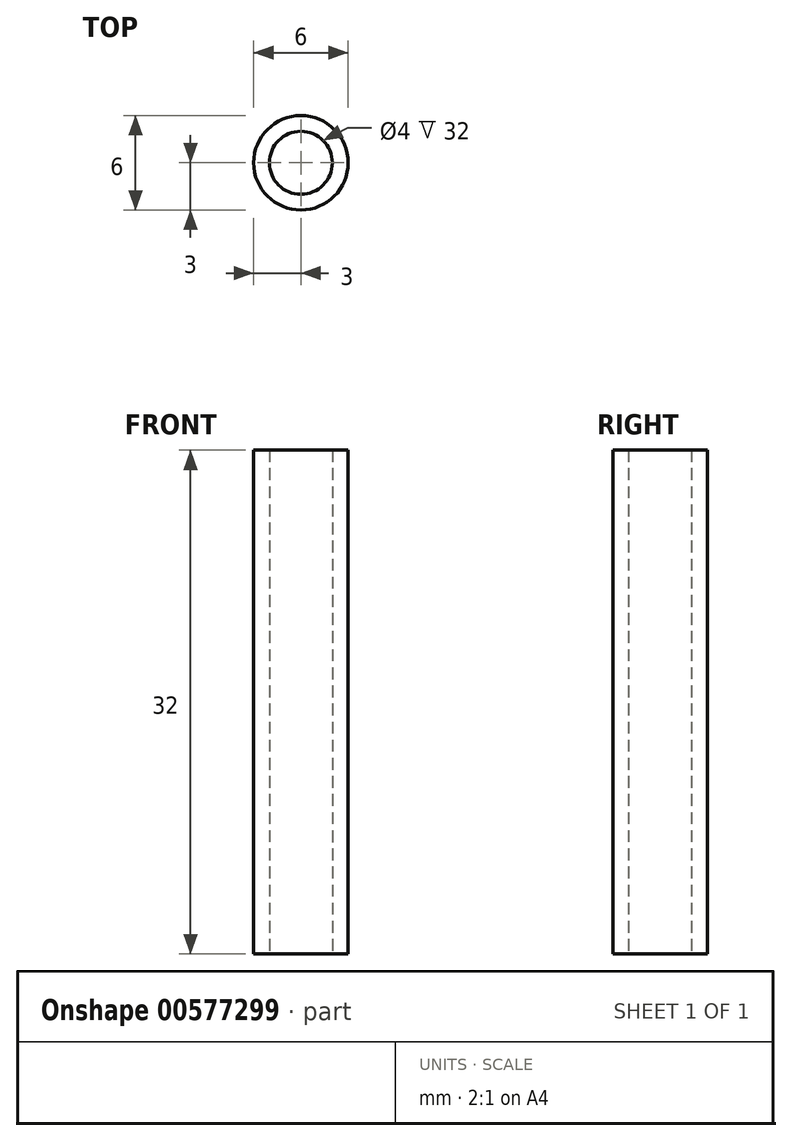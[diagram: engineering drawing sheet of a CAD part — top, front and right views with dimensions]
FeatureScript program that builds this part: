
annotation { "Feature Type Name" : "Feature", "Feature Type Description" : "" }
export const myFeature = defineFeature(function(context is Context, id is Id, definition is map)
    precondition{}
    {
        {
            var Q0;
            Q0=qCreatedBy(makeId("Top.planeOp"),FACE);
            var sketch = newSketch(context, id + "F0", { "sketchPlane" : qUnion([Q0])});
            skCircle(sketch, "E0", {"center": v(0, 0) * mm, "radius": 2 * mm});
            skCircle(sketch, "E1", {"center": v(0, 0) * mm, "radius": 3 * mm});
            skSolve(sketch);
        }
        {
            var Q0;
            Q0 = qSketchRegion(id + "F0", true);
            extrude(context, id + "F1", {"entities" : qUnion([Q0]), "depth" : 32 * mm, "offsetDistance" : 25 * mm});
        }
    });
